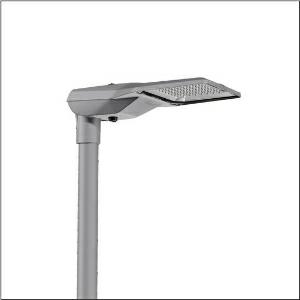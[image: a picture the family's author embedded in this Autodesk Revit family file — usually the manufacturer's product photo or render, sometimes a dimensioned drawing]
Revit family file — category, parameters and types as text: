
# Revit family: streetlight_sl_21_iq_midi___st1_0a_5xe3d41y08nb_87cf
name_source: partatom
category: Lighting Fixtures
units: mm (PartAtom-declared; Revit-internal decimal feet)

## family parameters
Cut with Voids When Loaded = No
Host = Face
Light Source = No
Part Type = Normal
Room Calculation Point = No
Round Connector Dimension = Use Diameter
Shared = No

## types (1)
- --- (1 x LED, 22330 lm, 136.6 W, 4000K)
    Apparent Load = 137 VA
    CIE Flux Codes = 40 73 97 100 100
    Color Rendering = 70
    Color Temperature = 4000K
    Default Elevation = 1800 mm
    Description = Streetlight SL 21 iQ midi, mast luminaire, primary light control with lens, of PMMA, primary optical cover: cover, of toughened safety glass, transparent, light distribution: ST1.0a, light emission: direct distribution, primary light characteristic: asymmetric, installation type: post-top, side-entry, LED, High Power LED, rated luminous flux: 22.330lm, luminous efficacy: 164lm/W, light colour: 740, colour temperature: 4000K, control gear: iQ-Street Remote, D4i with power reduction, control: pre-setting: logarithmic dimming characteristic, Street-Remote, Auto-Match, Temp-Guard, Lumen-Switch, Night-Set, Smart-Wire, Light-Fading, Desk-Remote (wireless, voltage-free reading and setting of iQ features in the workshop via application-optimized NFC function/RFID function), optimised constant luminous flux control (CLO 2.0), mains connection: 230..240V, AC, 50/60Hz, start of lifetime: 137W, end of service life: 144W, reduction: 62W, luminaire housing, of diecast aluminium, powder-coated, SITECO metallic grey (DB 702S), corrosivity category C5 high according to DIN EN ISO 12944, please order mast flange separately, inclination adjustable: 0°, 5°, 10°, 15°, sealing non-destructively replaceable, multi-level sealing system, length: 644mm, width: 335mm, height: 110mm, mast flange for spigot size: 42mm (side-entry): 5XC10008XM4, 60/48mm (side-entry/post-top): 5XC10108XM2, 76/60mm (side-entry/post-top): 5XC10108XM1, mounting height: 4..8m, Smart Interface below and above, protection rating (complete): IP66, insulation class (complete): insulation class II (safety insulation), certification: CE, ENEC, ENEC+, VDE, impact resistance: IK10, permissible operating ambient temperature for outdoor applications: -40..+50°C, standard-compliant lighting for roads and squares, packaging unit: 1 piece

Light Distribution: ST1.0a
    Height = 111 mm
    Lamp = 1 x LED
    Lamp Light Flux = 22330 lm
    Lamp Power = 136.6 W
    Lamp count = 1
    Length = 644 mm
    Luminous efficacy = 163 lm/W
    Manufacturer = Siteco
    ModVariant = No
    Model = 5XE3D41Y08NB
    Number of Poles = 1
    OnlyDefault = Yes
    Power Factor = 1
    Product Name = Streetlight SL 21 iQ midi | ST1.0a
    Product group = mast luminaire | pylon top
    ProductGroupID = 6100
    Protection Class = Protection class II
    Protection Degree = IP 66
    RLX_Detail_Level = 1
    RLX_Emergency_Light_Flux = 0 lm
    RLX_Emergency_Type = 0
    RLX_Emergency_Type_DB = No
    RlxData = <blob elided: 91133 chars, md5=bfa2e1ad>
    Socket = socket
    Standby Power = 0 W
    System Light Flux = 22330 lm
    System Power = 137 W
    Type Comments = factory setting: luminous flux: 100 % | dim-lin: 254 | 733 mA
    Type Image = l_1004304.jpg
    URL = http://relux.com
    VarID = @adj_113853
    Voltage = 0 V
    Weight = 0.00 kg
    Width = 336 mm

## geometry (parser evidence)
native form markers: Blend x4, Sweep x11
no freeform markers — native parametric forms only
